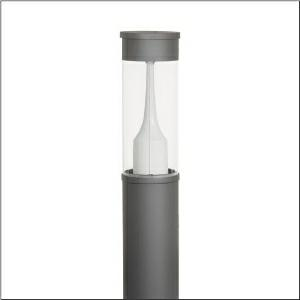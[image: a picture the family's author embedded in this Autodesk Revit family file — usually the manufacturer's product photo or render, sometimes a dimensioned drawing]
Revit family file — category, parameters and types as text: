
# Revit family: city-light_400_iq___p1_0a_5xa5305ff14h_0bc5
name_source: partatom
category: Lighting Fixtures
units: mm (PartAtom-declared; Revit-internal decimal feet)

## family parameters
Cut with Voids When Loaded = No
Host = Face
Light Source = No
Part Type = Normal
Room Calculation Point = No
Round Connector Dimension = Use Diameter
Shared = No

## types (1)
- --- (1 x LED, 1510 lm, 10.5 W, 3000K)
    Apparent Load = 11 VA
    CIE Flux Codes = 32 61 90 93 100
    Color Rendering = 70
    Color Temperature = 3000K
    Default Elevation = 1800 mm
    Description = City-Light 400 iQ, light pillar, Module 540 iQ-SR, primary light control with 3 zone facetted reflector, of plastic, silver coated, highly specular, structured, primary optical cover: cover, of PMMA, transparent, light distribution: P1.0a, primary light characteristic: strongly asymmetric, LED, High Power LED, rated luminous flux: 1.510lm, luminous efficacy: 144lm/W, light colour: 730, colour temperature: 3000K, control gear: iQ Street-Remote, control: Auto-Match, Temp-Guard, Lumen-Switch, Night-Set, Smart-Wire, Light-Fading, Desk-Remote (wireless, voltage-free reading and setting of iQ features in the workshop via application-optimized NFC function/RFID function), optimised constant luminous flux control (CLO 2.0), Street-Remote, pre-setting: logarithmic dimming characteristic, with terminal, 6-pole, max. 2.5mm², mains connection: 230..240V, AC, 50/60Hz, start of lifetime: 11W, end of service life: 11W, reduction: 5W, luminaire housing, cylindrical, of extruded aluminium section, coated, Siteco® metallic grey (DB 702S), length: 4.694mm, diameter: 200mm, Module 540 iQ-SR, traffic white (RAL 9016), equipment: standard, protection rating (complete): IP65, insulation class (complete): insulation class II (safety insulation), certification: CE, ENEC, VDE, packaging unit: 1 piece

Light Distribution: P1.0a
    Height = 500 mm
    Lamp = 1 x LED
    Lamp Light Flux = 1510 lm
    Lamp Power = 10.5 W
    Lamp count = 1
    Length = 200 mm  [stored 0.656168 ft]
    Luminous efficacy = 144 lm/W
    Manufacturer = Siteco
    ModVariant = No
    Model = 5XA5305FF14H
    Mounting Place = Floor
    Mounting Type = Freestanding
    Number of Poles = 1
    OnlyDefault = Yes
    Power Factor = 1
    Product Name = City-Light 400 iQ | P1.0a
    Product group = light pillar
    ProductGroupID = 1301
    Protection Class = Protection class II
    Protection Degree = IP 65
    RLX_Detail_Level = 1
    RLX_Emergency_Light_Flux = 0 lm
    RLX_Emergency_Type = 0
    RLX_Emergency_Type_DB = No
    RlxData = <blob elided: 75437 chars, md5=96584845>
    Socket = socket
    Standby Power = 0 W
    System Light Flux = 1510 lm
    System Power = 11 W
    Type Comments = factory setting: luminous flux: 100 % | dim-lin: 254 | 419 mA
    Type Image = l_1006914.jpg
    URL = http://relux.com
    VarID = @adj_180865
    Voltage = 0 V
    Weight = 0.00 kg
    Width = 0 mm  [stored 0 ft]

note: [stored X ft] marks values corroborated as IEEE doubles in the binary element streams (Revit-internal decimal feet)

## geometry (parser evidence)
native form markers: Blend x4, Sweep x10
no freeform markers — native parametric forms only
